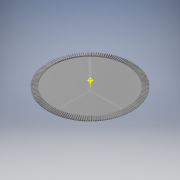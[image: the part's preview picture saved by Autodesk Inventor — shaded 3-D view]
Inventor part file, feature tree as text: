
AUTODESK INVENTOR PART (.ipt)
format: ipt  version: 2017 (Build 210142000, 142)  size: 1,876,480 bytes
history: native  units: mm
features: other x24, loft x2, pattern_circular x2, sketch x2, extrude x1
ambient origin geometry x6: Origin, XZ Plane, X Axis, Y Axis, Z Axis, Center Point
bodies: Solid1 (feature_tree)
feature tree (31):
  other  "Top Point"
  other  "Mesh Plane2"
  other  "Teeth Body"
  other  "Start Point"
  other  "Tooth Plane"
  other  "Start Sketch"
  other  "End Point"
  other  "3D Sketch Right"
  other  "End Plane Right"
  loft  "Loft Right"
  pattern_circular  "Circular Pattern Right"  [2 undecoded]
  other  "3D Sketch Left"
  other  "End Plane Left"
  loft  "Loft Left"
  pattern_circular  "Circular Pattern Left"  Angle=90.0deg  [1 undecoded]
  other  "Fix Body"
  extrude  "Extrusion1"  Depth=10.0mm
  other  "Mesh Plane"
  other  "Top Plane"
  other  "Teeth Body Sketch"
  other  "End Plane"
  other  "End Sketch"
  other  "Helical Curve Left"
  other  "End Sketch Left"
  other  "Body Sketch"
  sketch  "Sketch6"  dims[d0=330.2mm d1=329.501251mm]
  other  "Srf1"
  other  "Helical Curve Right"
  other  "End Sketch Right"
  sketch  "Sketch8"  dims[d2=330.78229mm d3=12.7mm d4=16.526741mm d5=90.0deg d7=493.522657mm d8=468.312989mm d9=1278.766519mm d11=12.9794mm d12=455.473429mm d15=432.207357mm d16=1180.177168mm d17=0.0mm d18=90.0deg d19=0.0mm d20=90.0deg d21=1300.0mm d22=360.0deg d26=408.108671mm d27=1.487752mm d28=330.2mm d29=-14.559197mm d30=455.473429mm d31=432.207357mm d32=1180.177168mm d35=0.0mm d37=0.0mm d39=0.0mm d40=90.0deg d41=1300.0mm d42=360.0deg d46=90.0deg d47=90.0deg d48=0.0mm d49=0.0mm d50=90.0deg d51=0.241661mm d52=0.0mm d53=0.0mm d54=0.0mm d56=17.556067mm d57=1444.576572mm d58=1436.641612mm d59=1333.203726mm d60=1325.880529mm d61=1333.203726mm d62=1325.880529mm d63=90.0deg d64=90.0deg d65=408.108671mm d66=31.5mm d67=330.2mm d68=-14.559197mm d69=1.487752mm d70=432.207357mm d71=1180.177168mm d72=455.473429mm d73=1325.880529mm d74=1333.203726mm d75=0.0mm d76=90.0deg d77=0.0mm d78=90.0deg d79=0.0mm d80=90.0deg d81=1300.0mm d82=360.0deg d84=10.0mm d85=20.0mm d86=20.0mm d87=10.0mm d88=0.0mm d89=0.0mm d90=304.8mm d91=25.4mm d92=0.0mm]
  other  "Pitch Diameter"
note: 3 required parameter values undecoded (feature->parameter linkage not recoverable at this tier; creation-order binding heuristic only, values carry confidence <= 0.55)
